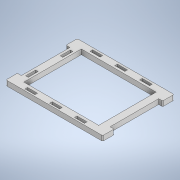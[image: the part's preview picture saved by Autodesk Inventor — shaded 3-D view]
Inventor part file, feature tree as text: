
AUTODESK INVENTOR PART (.ipt)
format: ipt  version: 2020 (Build 240168000, 168)  size: 180,736 bytes
history: native  units: mm
features: extrude x1, sketch x1
ambient origin geometry x8: Origin, YZ Plane, XZ Plane, XY Plane, X Axis, Y Axis, Z Axis, Center Point
bodies: Solid1 (feature_tree)
feature tree (2):
  extrude  "Extrusion1"  Depth=144.0mm
  sketch  "Sketch1"  dims[d0=179.0mm d1=144.0mm d2=151.0mm d3=116.0mm d4=8.0mm d5=23.0mm d6=8.0mm d7=23.0mm d8=8.0mm d9=23.0mm d10=8.0mm d11=23.0mm d12=20.2mm d13=5.2mm d14=4.15mm d15=13.0mm d16=30.0mm d18=50.0mm d19=20.0mm d21=131.5mm d24=2.0mm d25=5.2mm d26=20.2mm d27=4.0mm d28=13.0mm d29=20.0mm d31=70.0mm d32=10.0mm d34=10.0mm d36=10.0mm d37=0.0mm]
